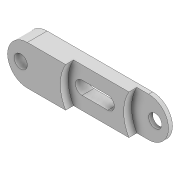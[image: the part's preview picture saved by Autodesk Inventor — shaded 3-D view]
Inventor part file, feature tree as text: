
AUTODESK INVENTOR PART (.ipt)
format: ipt  version: 2021 (Build 250183000, 183)  size: 192,512 bytes
history: native  units: mm
features: extrude x5, sketch x5, projected_geometry x3
ambient origin geometry x8: Origin, YZ Plane, XZ Plane, XY Plane, X Axis, Y Axis, Z Axis, Center Point
bodies: Solid1 (feature_tree)
feature tree (13):
  extrude  "Extrusion1"  Depth=10.0mm
  extrude  "Extrusion2"  Depth=10.0mm
  extrude  "Extrusion3"  Depth=15.0mm
  extrude  "Extrusion4"  TaperAngle=0.0deg  [1 undecoded]
  extrude  "Extrusion5"  Depth=6.0mm
  sketch  "Sketch1"  dims[d1=30.0mm d14=10.0mm]
  sketch  "Sketch2"  dims[d15=10.0mm d16=10.0mm]
  projected_geometry  "Projected Loop1"
  sketch  "Sketch3"  dims[d17=90.0mm d18=15.0mm]
  projected_geometry  "Projected Loop2"
  sketch  "Sketch4"  dims[d19=3.0mm d20=0.0mm]
  projected_geometry  "Projected Loop3"
  sketch  "Sketch5"  dims[d21=15.0mm d22=6.0mm d23=0.0mm d26=40.5mm d27=30.0mm d28=10.0mm d29=6.0mm d30=0.0mm d32=60.0mm d33=12.0mm d34=60.0mm d35=60.0mm d36=6.0mm d37=0.0mm d38=5.0mm d39=40.5mm d40=20.25mm d41=0.1mm d42=0.0mm]
note: 1 required parameter value undecoded (feature->parameter linkage not recoverable at this tier; creation-order binding heuristic only, values carry confidence <= 0.55)
